# Revit family: 353_Inspect chamb TK 400_160-2200
name_source: partatom
category: Plumbing Fixtures
units: mm (PartAtom-declared; Revit-internal decimal feet)

## family parameters
Always vertical = Yes
Cut with Voids When Loaded = No
Part Type = Normal
Room Calculation Point = No
Round Connector Dimension = Use Diameter
Shared = No
Work Plane-Based = No

## types (1)
- Inspection chamber TK400/160-2200 p/n 086332
    BD = 400 mm  [stored 1.31234 ft]
    CAT0 = Yes
    CLBTZ = 0 mm  [stored 0 ft]
    CL_Location_5000 = 5000 mm  [stored 16.4042 ft]
    D = 160 mm
    D1 = 480 mm
    Description = Inspection chamber TK400/160-2200 p/n:086332
    L = 560 mm  [stored 1.83727 ft]
    L2 = 280 mm  [stored 0.918635 ft]
    L2__ve = -280 mm  [stored -0.918635 ft]
    L__ve = -560 mm  [stored -1.83727 ft]
    MC Product Code = Inspection chamber TK400/160-2200 p/n:086332
    Manufacturer = Pipelife
    QmdConnectorList = 651;D;652;D;653;D;654;D
    R = 80 mm  [stored 0.262467 ft]
    URL = http://www.pipelife.fi
    X1 = 198 mm
    Z1 = 99 mm  [stored 0.324803 ft]
    Z1__ve = -99 mm  [stored -0.324803 ft]
    ZZ = 22 mm  [stored 0.0721785 ft]
    magiPartTypeId = 353
    magiProductFamilyId = Inspect chamb TK 400/160-2200
    magiProductId = Inspect chamb TK 400/160-2200

note: [stored X ft] marks values corroborated as IEEE doubles in the binary element streams (Revit-internal decimal feet)

## geometry (parser evidence)
native form markers: Sweep x2
no freeform markers — native parametric forms only
